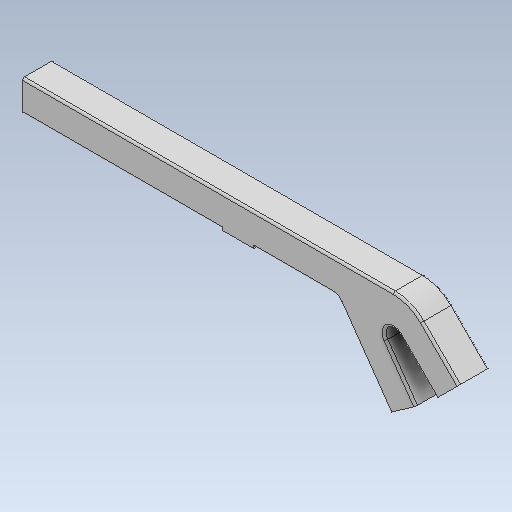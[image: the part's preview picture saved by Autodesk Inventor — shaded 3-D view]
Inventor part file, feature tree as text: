
AUTODESK INVENTOR PART (.ipt)
format: ipt  version: 2021 (Build 250183000, 183)  size: 256,512 bytes
history: native  units: mm
features: extrude x5, sketch x4, fillet x3
ambient origin geometry x8: Origin, YZ Plane, XZ Plane, XY Plane, X Axis, Y Axis, Z Axis, Center Point
bodies: Solid1 (feature_tree)
feature tree (12):
  extrude  "Extrusion1"  Depth=30.0mm
  extrude  "Extrusion4"  Depth=9.0mm
  fillet  "Fillet1"  Radius=30.0mm
  extrude  "Extrusion5"  Depth=9.0mm
  fillet  "Fillet2"  Radius=150.0mm
  extrude  "Extrusion6"  Depth=2.0mm
  extrude  "Extrusion7"  Depth=2.0mm
  fillet  "Fillet3"  Radius=30.0mm
  sketch  "Sketch4"  dims[d31=30.0mm d32=0.0mm d38=30.0mm]
  sketch  "Sketch5"  dims[d39=30.0mm d40=9.0mm d47=30.0mm]
  sketch  "Sketch6"  dims[d53=9.0mm d56=300.0mm d58=150.0mm]
  sketch  "Sketch7"  dims[d59=50.0mm d60=6.108652mm d61=75.0mm d62=30.0mm d63=15.0mm d64=1.0mm d65=30.0mm d66=0.0mm d67=2.0mm d68=2.5mm d69=2.5mm d70=2.5mm d71=2.5mm d72=350.0mm d73=0.0mm d74=2.0mm d75=2.5mm d76=2.5mm d77=2.5mm d78=2.5mm d79=50.0mm d80=0.0mm d81=2.5mm d82=2.5mm d83=2.5mm d84=2.5mm d85=50.0mm d86=0.0mm d87=2.0mm d88=45.0deg]
